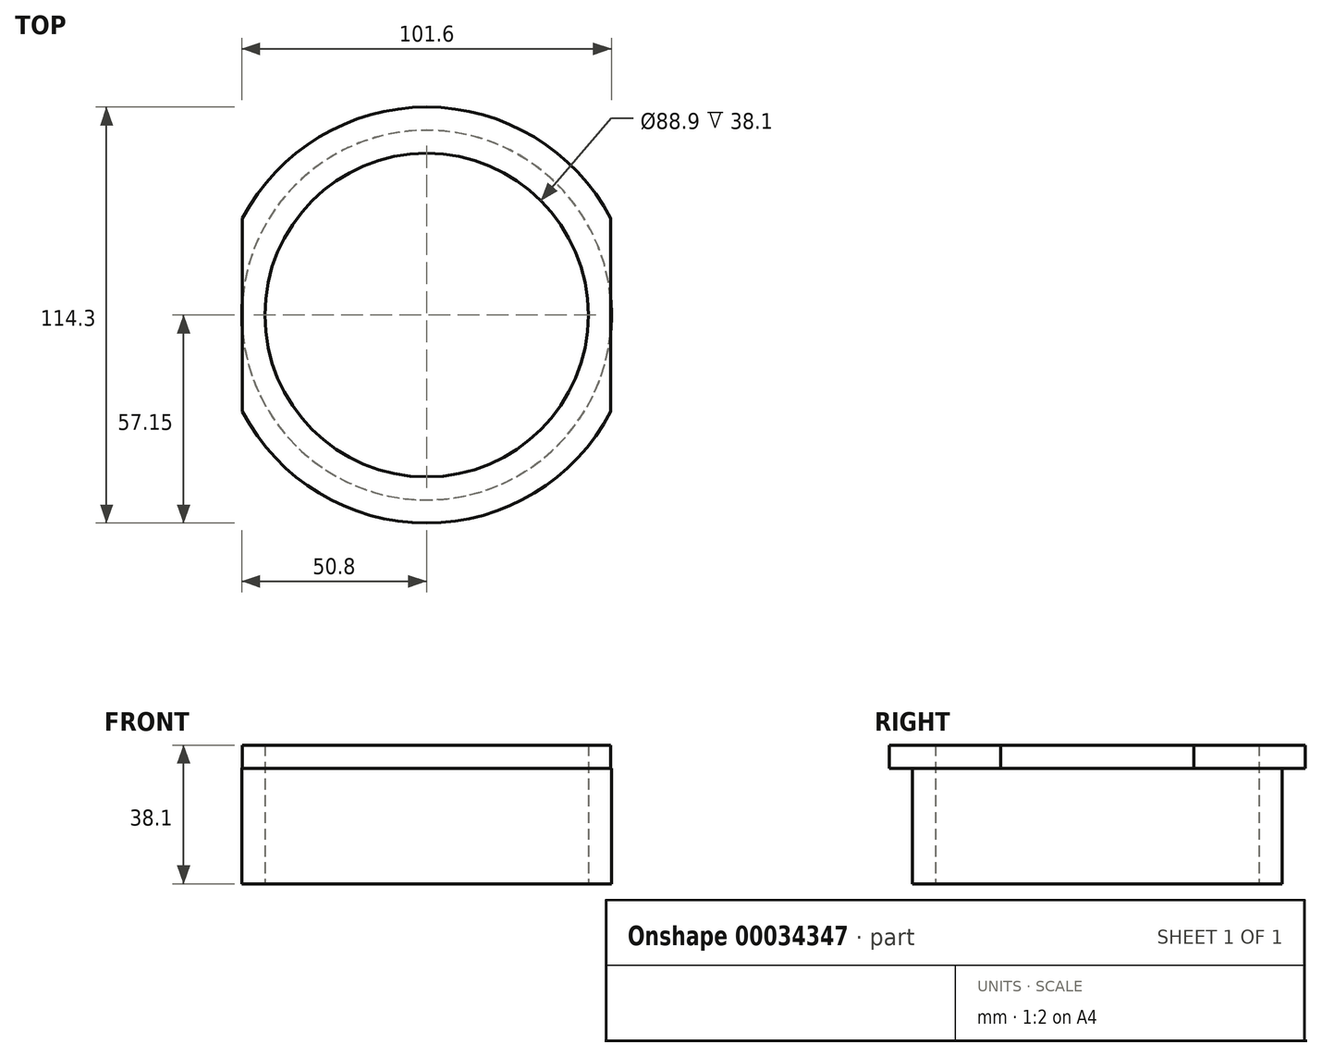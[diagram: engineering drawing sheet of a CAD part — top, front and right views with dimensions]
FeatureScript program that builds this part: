
annotation { "Feature Type Name" : "Feature", "Feature Type Description" : "" }
export const myFeature = defineFeature(function(context is Context, id is Id, definition is map)
    precondition{}
    {
        {
            var Q0;
            Q0=qCreatedBy(makeId("Top.planeOp"),FACE);
            var sketch = newSketch(context, id + "F0", { "sketchPlane" : qUnion([Q0])});
            skCircle(sketch, "E0", {"center": v(0, 0) * mm, "radius": 50.8 * mm});
            skCircle(sketch, "E1.0", {"center": v(0, 0) * mm, "radius": 44.45 * mm});
            skSolve(sketch);
        }
        {
            var Q0;
            Q0=makeQuery(id+"F0.imprint","IMPRINT",FACE,{"disambiguationData":[TD([[makeQuery(id+"F0.imprint","IMPRINT",EDGE,{"derivedFrom":sQuery(id+"F0.wireOp",EDGE,"E0")}),1.0]])]});
            extrude(context, id + "F1", {"entities" : qUnion([Q0]), "depth" : 31.75 * mm});
        }
        {
            var Q0;
            Q0=makeQuery(id+"F1.opExtrude","CAP_FACE",FACE,{"disambiguationData":[OSD([sQuery(id+"F0.wireOp",EDGE,"E0"),sQuery(id+"F0.wireOp",EDGE,"E1.0")])],"isStart":false});
            var sketch = newSketch(context, id + "F2", { "sketchPlane" : qUnion([Q0])});
            skArc(sketch, "E2.0", {"start": v(-50.61, -26.54) * mm, "mid": v(0, -57.15) * mm, "end": v(50.61, -26.54) * mm});
            skArc(sketch, "E3.trimOffspring", {"start": v(50.61, 26.54) * mm, "mid": v(0, 57.15) * mm, "end": v(-50.61, 26.54) * mm});
            skLineSegment(sketch, "E4.0", {"start": v(50.61, -26.54) * mm, "end": v(50.61, 26.54) * mm});
            skLineSegment(sketch, "E5.0", {"start": v(-50.61, -1.07) * mm, "end": v(-50.61, -26.54) * mm});
            skLineSegment(sketch, "E5.1", {"start": v(-50.61, -1.07) * mm, "end": v(-50.61, 26.54) * mm});
            skSolve(sketch);
        }
        {
            var Q0;
            Q0 = qSketchRegion(id + "F2", true);
            extrude(context, id + "F3", {"entities" : qUnion([Q0]), "operationType" : NewBodyOperationType.ADD, "depth" : 6.35 * mm});
        }
        {
            var Q0;
            Q0=makeQuery(id+"F3.boolean.opBoolean","SPLIT",FACE,{"disambiguationData":[TD([makeQuery(id+"F1.opExtrude","SWEPT_FACE",FACE,{"disambiguationData":[OSD([sQuery(id+"F0.wireOp",EDGE,"E1.0")])]})])],"derivedFrom":makeQuery(id+"F3.opExtrude","CAP_FACE",FACE,{"disambiguationData":[OSD([sQuery(id+"F2.wireOp",EDGE,"E2.0"),sQuery(id+"F2.wireOp",EDGE,"ef11bcc9-c215-4255-b367-998e49c748a7.0"),sQuery(id+"F2.wireOp",EDGE,"ef11bcc9-c215-4255-b367-998e49c748a7.1"),sQuery(id+"F2.wireOp",EDGE,"301642ca-1711-41eb-a73b-8d7c0db3094d.0"),sQuery(id+"F2.wireOp",EDGE,"E3.trimOffspring")])],"isStart":true})});
            var sketch = newSketch(context, id + "F4", { "sketchPlane" : qUnion([Q0])});
            skCircle(sketch, "E6.0", {"center": v(0, 0) * mm, "radius": 44.45 * mm});
            skSolve(sketch);
        }
        {
            var Q0;
            Q0=makeQuery(id+"F4.imprint","IMPRINT",FACE,{"disambiguationData":[TD([[makeQuery(id+"F4.imprint","IMPRINT",EDGE,{"derivedFrom":sQuery(id+"F4.wireOp",EDGE,"E6.0")}),-1.0]])]});
            var Q1;
            Q1=sQuery(id+"F4.wireOp",EDGE,"E6.0");
            extrude(context, id + "F5", {"entities" : qUnion([Q0]), "operationType" : NewBodyOperationType.REMOVE, "surfaceEntities" : qUnion([Q1]), "oppositeDirection" : true, "depth" : 25.4 * mm});
        }
    });
